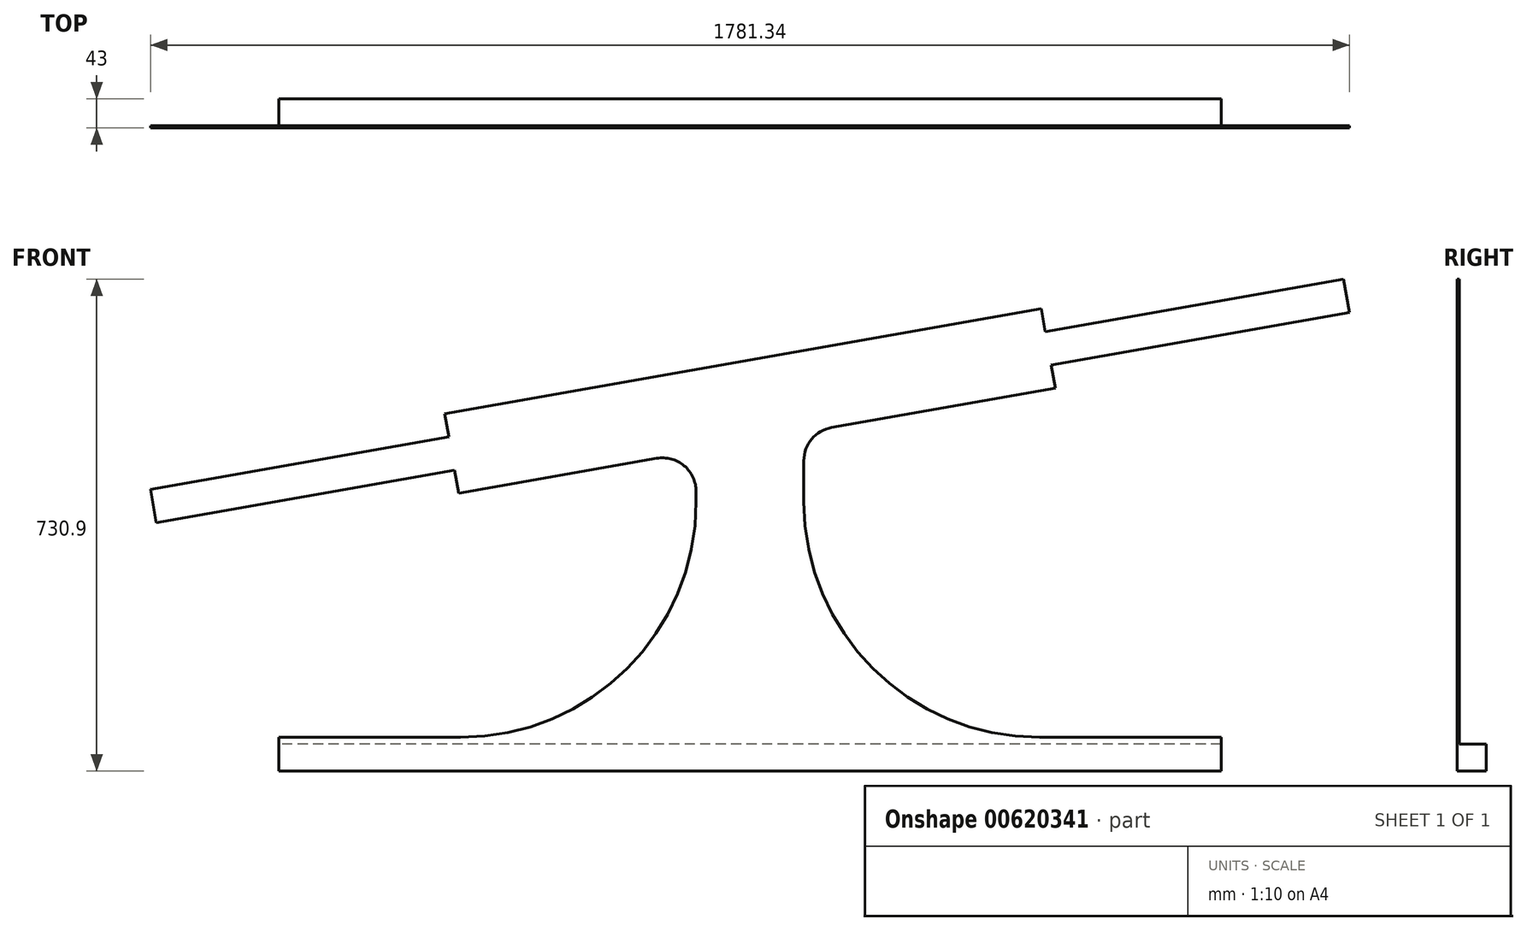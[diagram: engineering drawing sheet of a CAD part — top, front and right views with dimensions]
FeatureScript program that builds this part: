
annotation { "Feature Type Name" : "Feature", "Feature Type Description" : "" }
export const myFeature = defineFeature(function(context is Context, id is Id, definition is map)
    precondition{}
    {
        {
            var Q0;
            Q0=qCreatedBy(makeId("Front.planeOp"),FACE);
            var sketch = newSketch(context, id + "F0", { "sketchPlane" : qUnion([Q0])});
            skLineSegment(sketch, "E0", {"start": v(-80, 550) * mm, "end": v(-80, 400) * mm});
            skLineSegment(sketch, "E1", {"start": v(80, 550) * mm, "end": v(80, 400) * mm});
            skLineSegment(sketch, "E2", {"start": v(-80, 550) * mm, "end": v(80, 550) * mm});
            skLineSegment(sketch, "E3", {"start": v(-700, 50) * mm, "end": v(-430, 50) * mm});
            skLineSegment(sketch, "E4", {"start": v(700, 50) * mm, "end": v(430, 50) * mm});
            skArc(sketch, "E5", {"start": v(-430, 50) * mm, "mid": v(-182.51, 152.51) * mm, "end": v(-80, 400) * mm});
            skArc(sketch, "E6", {"start": v(80, 400) * mm, "mid": v(182.51, 152.51) * mm, "end": v(430, 50) * mm});
            skLineSegment(sketch, "E7", {"start": v(-443.16, 471.86) * mm, "end": v(443.16, 628.14) * mm});
            skCircle(sketch, "E8", {"center": v(-443.16, 471.86) * mm, "radius": 60 * mm});
            skCircle(sketch, "E9", {"center": v(443.16, 628.14) * mm, "radius": 60 * mm});
            skLineSegment(sketch, "E10", {"start": v(-10.42, 609.09) * mm, "end": v(0, 550) * mm});
            skPoint(sketch, "E11.end.orphan", {"position": v(-650.54, 496.22) * mm});
            skPoint(sketch, "E12.start.orphan", {"position": v(629.7, 721.96) * mm});
            skLineSegment(sketch, "E13", {"start": v(432.74, 687.23) * mm, "end": v(-453.58, 530.95) * mm});
            skLineSegment(sketch, "E14", {"start": v(-432.74, 412.77) * mm, "end": v(453.58, 569.05) * mm});
            skLineSegment(sketch, "E15", {"start": v(881.99, 730.9) * mm, "end": v(-890.67, 418.34) * mm});
            skLineSegment(sketch, "E16", {"start": v(-890.67, 418.34) * mm, "end": v(-881.99, 369.1) * mm});
            skLineSegment(sketch, "E17", {"start": v(-881.99, 369.1) * mm, "end": v(890.67, 681.66) * mm});
            skLineSegment(sketch, "E18", {"start": v(890.67, 681.66) * mm, "end": v(881.99, 730.9) * mm});
            skLineSegment(sketch, "E19", {"start": v(-453.58, 530.95) * mm, "end": v(-432.74, 412.77) * mm});
            skLineSegment(sketch, "E20", {"start": v(432.74, 687.23) * mm, "end": v(453.58, 569.05) * mm});
            skLineSegment(sketch, "E21", {"start": v(-700, 50) * mm, "end": v(-700, 0) * mm});
            skLineSegment(sketch, "E22", {"start": v(-700, 0) * mm, "end": v(700, 0) * mm});
            skLineSegment(sketch, "E23", {"start": v(700, 0) * mm, "end": v(700, 50) * mm});
            skSolve(sketch);
        }
        {
            var Q0;
            Q0=makeQuery(id+"F0.imprint","IMPRINT",FACE,{"disambiguationData":[TD([[makeQuery(id+"F0.imprint","IMPRINT",EDGE,{"derivedFrom":sQuery(id+"F0.wireOp",EDGE,"E3")}),-1.0]])]});
            var Q1;
            {var subQ5=sQuery(id+"F0.wireOp",EDGE,"E16");Q1=makeQuery(id+"F0.imprint","IMPRINT",FACE,{"disambiguationData":[TD([[makeQuery(id+"F0.imprint","IMPRINT",EDGE,{"derivedFrom":subQ5}),1.0]])]});}
            var Q2;
            {var subQ2=sQuery(id+"F0.wireOp",EDGE,"E15");var subQ5=sQuery(id+"F0.wireOp",EDGE,"E8");var subQ8=makeQuery(id+"F0.imprint","INTERSECT",VERTEX,{"disambiguationData":[OD(0.0)],"derivedFrom":[subQ5,subQ2]});Q2=makeQuery(id+"F0.imprint","IMPRINT",FACE,{"disambiguationData":[TD([[makeQuery(id+"F0.imprint","IMPRINT",EDGE,{"disambiguationData":[TD([[subQ8,-1.0]])],"derivedFrom":subQ5}),1.0]])]});}
            var Q3;
            {var subQ0=sQuery(id+"F0.wireOp",EDGE,"E19");var subQ1=sQuery(id+"F0.wireOp",EDGE,"E7");var subQ2=makeQuery(id+"F0.imprint","INTERSECT",VERTEX,{"derivedFrom":[subQ1,subQ0]});Q3=makeQuery(id+"F0.imprint","IMPRINT",FACE,{"disambiguationData":[TD([[makeQuery(id+"F0.imprint","IMPRINT",EDGE,{"disambiguationData":[TD([[subQ2,-1.0]])],"derivedFrom":subQ1}),-1.0]])]});}
            var Q4;
            {var subQ0=sQuery(id+"F0.wireOp",EDGE,"E19");var subQ1=sQuery(id+"F0.wireOp",EDGE,"E7");var subQ2=makeQuery(id+"F0.imprint","INTERSECT",VERTEX,{"derivedFrom":[subQ1,subQ0]});Q4=makeQuery(id+"F0.imprint","IMPRINT",FACE,{"disambiguationData":[TD([[makeQuery(id+"F0.imprint","IMPRINT",EDGE,{"disambiguationData":[TD([[subQ2,-1.0]])],"derivedFrom":subQ1}),1.0]])]});}
            var Q5;
            {var subQ0=sQuery(id+"F0.wireOp",EDGE,"E13");var subQ5=sQuery(id+"F0.wireOp",EDGE,"E10");var subQ6=makeQuery(id+"F0.imprint","INTERSECT",VERTEX,{"derivedFrom":[subQ5,subQ0]});Q5=makeQuery(id+"F0.imprint","IMPRINT",FACE,{"disambiguationData":[TD([[makeQuery(id+"F0.imprint","IMPRINT",EDGE,{"disambiguationData":[TD([[subQ6,-1.0]])],"derivedFrom":subQ5}),-1.0]])]});}
            var Q6;
            {var subQ5=sQuery(id+"F0.wireOp",EDGE,"E2");var subQ6=sQuery(id+"F0.wireOp",EDGE,"E0");var subQ7=makeQuery(id+"F0.imprint","INTERSECT",VERTEX,{"derivedFrom":[subQ6,subQ5]});Q6=makeQuery(id+"F0.imprint","IMPRINT",FACE,{"disambiguationData":[TD([[makeQuery(id+"F0.imprint","IMPRINT",EDGE,{"disambiguationData":[TD([[subQ7,-1.0]])],"derivedFrom":subQ6}),-1.0]])]});}
            var Q7;
            {var subQ0=sQuery(id+"F0.wireOp",EDGE,"E7");var subQ1=sQuery(id+"F0.wireOp",EDGE,"E0");var subQ2=makeQuery(id+"F0.imprint","INTERSECT",VERTEX,{"derivedFrom":[subQ1,subQ0]});Q7=makeQuery(id+"F0.imprint","IMPRINT",FACE,{"disambiguationData":[TD([[makeQuery(id+"F0.imprint","IMPRINT",EDGE,{"disambiguationData":[TD([[subQ2,-1.0]])],"derivedFrom":subQ1}),-1.0]])]});}
            var Q8;
            {var subQ0=sQuery(id+"F0.wireOp",EDGE,"E14");var subQ1=sQuery(id+"F0.wireOp",EDGE,"E0");var subQ2=makeQuery(id+"F0.imprint","INTERSECT",VERTEX,{"derivedFrom":[subQ1,subQ0]});Q8=makeQuery(id+"F0.imprint","IMPRINT",FACE,{"disambiguationData":[TD([[makeQuery(id+"F0.imprint","IMPRINT",EDGE,{"disambiguationData":[TD([[subQ2,1.0]])],"derivedFrom":subQ1}),-1.0]])]});}
            var Q9;
            {var subQ0=sQuery(id+"F0.wireOp",EDGE,"E14");var subQ1=sQuery(id+"F0.wireOp",EDGE,"E0");var subQ2=makeQuery(id+"F0.imprint","INTERSECT",VERTEX,{"derivedFrom":[subQ1,subQ0]});Q9=makeQuery(id+"F0.imprint","IMPRINT",FACE,{"disambiguationData":[TD([[makeQuery(id+"F0.imprint","IMPRINT",EDGE,{"disambiguationData":[TD([[subQ2,1.0]])],"derivedFrom":subQ1}),1.0]])]});}
            var Q10;
            {var subQ0=sQuery(id+"F0.wireOp",EDGE,"E7");var subQ3=sQuery(id+"F0.wireOp",EDGE,"E0");var subQ4=makeQuery(id+"F0.imprint","INTERSECT",VERTEX,{"derivedFrom":[subQ3,subQ0]});Q10=makeQuery(id+"F0.imprint","IMPRINT",FACE,{"disambiguationData":[TD([[makeQuery(id+"F0.imprint","IMPRINT",EDGE,{"disambiguationData":[TD([[subQ4,-1.0]])],"derivedFrom":subQ3}),1.0]])]});}
            var Q11;
            {var subQ0=sQuery(id+"F0.wireOp",EDGE,"E2");var subQ1=sQuery(id+"F0.wireOp",EDGE,"E0");var subQ2=makeQuery(id+"F0.imprint","INTERSECT",VERTEX,{"derivedFrom":[subQ1,subQ0]});Q11=makeQuery(id+"F0.imprint","IMPRINT",FACE,{"disambiguationData":[TD([[makeQuery(id+"F0.imprint","IMPRINT",EDGE,{"disambiguationData":[TD([[subQ2,-1.0]])],"derivedFrom":subQ1}),1.0]])]});}
            var Q12;
            {var subQ0=sQuery(id+"F0.wireOp",EDGE,"E20");var subQ1=sQuery(id+"F0.wireOp",EDGE,"E7");var subQ2=makeQuery(id+"F0.imprint","INTERSECT",VERTEX,{"derivedFrom":[subQ1,subQ0]});Q12=makeQuery(id+"F0.imprint","IMPRINT",FACE,{"disambiguationData":[TD([[makeQuery(id+"F0.imprint","IMPRINT",EDGE,{"disambiguationData":[TD([[subQ2,1.0]])],"derivedFrom":subQ1}),-1.0]])]});}
            var Q13;
            {var subQ1=sQuery(id+"F0.wireOp",EDGE,"E7");var subQ3=sQuery(id+"F0.wireOp",EDGE,"E9");var subQ4=makeQuery(id+"F0.imprint","INTERSECT",VERTEX,{"derivedFrom":[subQ1,subQ3]});Q13=makeQuery(id+"F0.imprint","IMPRINT",FACE,{"disambiguationData":[TD([[makeQuery(id+"F0.imprint","IMPRINT",EDGE,{"disambiguationData":[TD([[subQ4,1.0]])],"derivedFrom":subQ3}),-1.0]])]});}
            var Q14;
            {var subQ1=sQuery(id+"F0.wireOp",EDGE,"E9");var subQ3=sQuery(id+"F0.wireOp",EDGE,"E17");var subQ4=makeQuery(id+"F0.imprint","INTERSECT",VERTEX,{"disambiguationData":[OD(1.0)],"derivedFrom":[subQ1,subQ3]});Q14=makeQuery(id+"F0.imprint","IMPRINT",FACE,{"disambiguationData":[TD([[makeQuery(id+"F0.imprint","IMPRINT",EDGE,{"disambiguationData":[TD([[subQ4,-1.0]])],"derivedFrom":subQ3}),-1.0]])]});}
            var Q15;
            {var subQ1=sQuery(id+"F0.wireOp",EDGE,"E9");var subQ3=sQuery(id+"F0.wireOp",EDGE,"E15");var subQ4=makeQuery(id+"F0.imprint","INTERSECT",VERTEX,{"disambiguationData":[OD(1.0)],"derivedFrom":[subQ1,subQ3]});Q15=makeQuery(id+"F0.imprint","IMPRINT",FACE,{"disambiguationData":[TD([[makeQuery(id+"F0.imprint","IMPRINT",EDGE,{"disambiguationData":[TD([[subQ4,1.0]])],"derivedFrom":subQ3}),-1.0]])]});}
            var Q16;
            {var subQ0=sQuery(id+"F0.wireOp",EDGE,"E14");var subQ1=sQuery(id+"F0.wireOp",EDGE,"E1");var subQ2=makeQuery(id+"F0.imprint","INTERSECT",VERTEX,{"derivedFrom":[subQ1,subQ0]});Q16=makeQuery(id+"F0.imprint","IMPRINT",FACE,{"disambiguationData":[TD([[makeQuery(id+"F0.imprint","IMPRINT",EDGE,{"disambiguationData":[TD([[subQ2,1.0]])],"derivedFrom":subQ1}),1.0]])]});}
            var Q17;
            {var subQ0=sQuery(id+"F0.wireOp",EDGE,"E20");var subQ1=sQuery(id+"F0.wireOp",EDGE,"E7");var subQ2=makeQuery(id+"F0.imprint","INTERSECT",VERTEX,{"derivedFrom":[subQ1,subQ0]});Q17=makeQuery(id+"F0.imprint","IMPRINT",FACE,{"disambiguationData":[TD([[makeQuery(id+"F0.imprint","IMPRINT",EDGE,{"disambiguationData":[TD([[subQ2,1.0]])],"derivedFrom":subQ1}),1.0]])]});}
            var Q18;
            {var subQ1=sQuery(id+"F0.wireOp",EDGE,"E2");var subQ7=sQuery(id+"F0.wireOp",EDGE,"E1");var subQ8=makeQuery(id+"F0.imprint","INTERSECT",VERTEX,{"derivedFrom":[subQ7,subQ1]});Q18=makeQuery(id+"F0.imprint","IMPRINT",FACE,{"disambiguationData":[TD([[makeQuery(id+"F0.imprint","IMPRINT",EDGE,{"disambiguationData":[TD([[subQ8,-1.0]])],"derivedFrom":subQ7}),1.0]])]});}
            var Q19;
            {var subQ0=sQuery(id+"F0.wireOp",EDGE,"E13");var subQ5=sQuery(id+"F0.wireOp",EDGE,"E10");var subQ6=makeQuery(id+"F0.imprint","INTERSECT",VERTEX,{"derivedFrom":[subQ5,subQ0]});Q19=makeQuery(id+"F0.imprint","IMPRINT",FACE,{"disambiguationData":[TD([[makeQuery(id+"F0.imprint","IMPRINT",EDGE,{"disambiguationData":[TD([[subQ6,-1.0]])],"derivedFrom":subQ5}),1.0]])]});}
            var Q20;
            {var subQ5=sQuery(id+"F0.wireOp",EDGE,"E18");Q20=makeQuery(id+"F0.imprint","IMPRINT",FACE,{"disambiguationData":[TD([[makeQuery(id+"F0.imprint","IMPRINT",EDGE,{"derivedFrom":subQ5}),1.0]])]});}
            var Q21;
            {var subQ2=sQuery(id+"F0.wireOp",EDGE,"E15");var subQ5=sQuery(id+"F0.wireOp",EDGE,"E9");var subQ8=makeQuery(id+"F0.imprint","INTERSECT",VERTEX,{"disambiguationData":[OD(0.0)],"derivedFrom":[subQ5,subQ2]});Q21=makeQuery(id+"F0.imprint","IMPRINT",FACE,{"disambiguationData":[TD([[makeQuery(id+"F0.imprint","IMPRINT",EDGE,{"disambiguationData":[TD([[subQ8,1.0]])],"derivedFrom":subQ5}),1.0]])]});}
            var Q22;
            {var subQ1=sQuery(id+"F0.wireOp",EDGE,"E8");var subQ3=sQuery(id+"F0.wireOp",EDGE,"E15");var subQ4=makeQuery(id+"F0.imprint","INTERSECT",VERTEX,{"disambiguationData":[OD(1.0)],"derivedFrom":[subQ1,subQ3]});Q22=makeQuery(id+"F0.imprint","IMPRINT",FACE,{"disambiguationData":[TD([[makeQuery(id+"F0.imprint","IMPRINT",EDGE,{"disambiguationData":[TD([[subQ4,-1.0]])],"derivedFrom":subQ3}),-1.0]])]});}
            var Q23;
            {var subQ1=sQuery(id+"F0.wireOp",EDGE,"E8");var subQ3=sQuery(id+"F0.wireOp",EDGE,"E17");var subQ4=makeQuery(id+"F0.imprint","INTERSECT",VERTEX,{"disambiguationData":[OD(1.0)],"derivedFrom":[subQ1,subQ3]});Q23=makeQuery(id+"F0.imprint","IMPRINT",FACE,{"disambiguationData":[TD([[makeQuery(id+"F0.imprint","IMPRINT",EDGE,{"disambiguationData":[TD([[subQ4,1.0]])],"derivedFrom":subQ3}),-1.0]])]});}
            extrude(context, id + "F1", {"entities" : qUnion([Q0, Q1, Q2, Q3, Q4, Q5, Q6, Q7, Q8, Q9, Q10, Q11, Q12, Q13, Q14, Q15, Q16, Q17, Q18, Q19, Q20, Q21, Q22, Q23]), "depth" : 3 * mm, "offsetDistance" : 25 * mm});
        }
        {
            var Q0;
            Q0=makeQuery(id+"F1.opExtrude","SWEPT_EDGE",EDGE,{"disambiguationData":[OSD([sQuery(id+"F0.wireOp",EDGE,"E0"),sQuery(id+"F0.wireOp",EDGE,"E14")])]});
            var Q1;
            Q1=makeQuery(id+"F1.opExtrude","SWEPT_EDGE",EDGE,{"disambiguationData":[OSD([sQuery(id+"F0.wireOp",EDGE,"E1"),sQuery(id+"F0.wireOp",EDGE,"E14")])]});
            fillet(context, id + "F2", {"entities" : qUnion([Q0, Q1]), "radius" : 50 * mm, "tangentPropagation" : true, "allowEdgeOverflow" : false});
        }
        {
            var Q0;
            Q0=makeQuery(id+"F0.imprint","IMPRINT",FACE,{"disambiguationData":[TD([[makeQuery(id+"F0.imprint","IMPRINT",EDGE,{"derivedFrom":sQuery(id+"F0.wireOp",EDGE,"E3")}),-1.0]])]});
            var sketch = newSketch(context, id + "F3", { "sketchPlane" : qUnion([Q0])});
            skLineSegment(sketch, "E24.bottom", {"start": v(700, 0) * mm, "end": v(-700, 0) * mm});
            skLineSegment(sketch, "E24.top", {"start": v(700, 40) * mm, "end": v(-700, 40) * mm});
            skLineSegment(sketch, "E24.left", {"start": v(700, 0) * mm, "end": v(700, 40) * mm});
            skLineSegment(sketch, "E24.right", {"start": v(-700, 0) * mm, "end": v(-700, 40) * mm});
            skSolve(sketch);
        }
        {
            var Q0;
            Q0=makeQuery(id+"F3.imprint","IMPRINT",FACE,{"disambiguationData":[TD([[makeQuery(id+"F3.imprint","IMPRINT",EDGE,{"derivedFrom":sQuery(id+"F3.wireOp",EDGE,"E24.bottom")}),1.0]])]});
            extrude(context, id + "F4", {"entities" : qUnion([Q0]), "operationType" : NewBodyOperationType.ADD, "oppositeDirection" : true, "depth" : 40 * mm, "offsetDistance" : 25 * mm});
        }
    });
